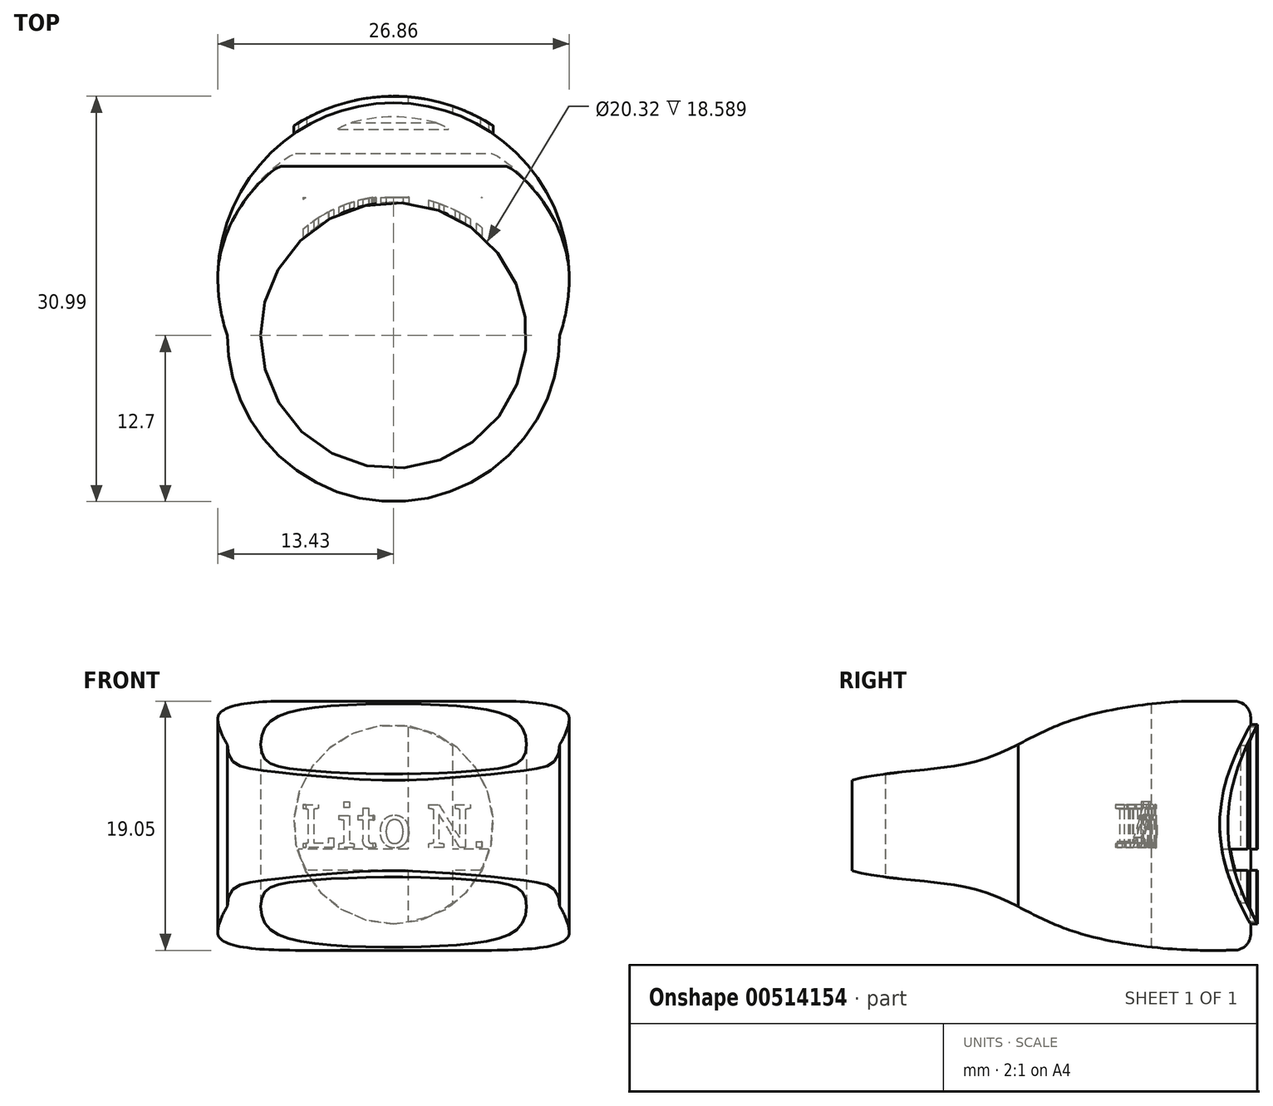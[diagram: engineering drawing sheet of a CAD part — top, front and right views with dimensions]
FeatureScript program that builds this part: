
annotation { "Feature Type Name" : "Feature", "Feature Type Description" : "" }
export const myFeature = defineFeature(function(context is Context, id is Id, definition is map)
    precondition{}
    {
        {
            var Q0;
            Q0=qCreatedBy(makeId("Top.planeOp"),FACE);
            var sketch = newSketch(context, id + "F0", { "sketchPlane" : qUnion([Q0])});
            skCircle(sketch, "E0", {"center": v(0, 0) * mm, "radius": 10.16 * mm});
            skArc(sketch, "E1", {"start": v(-12.7, 0) * mm, "mid": v(0, -12.7) * mm, "end": v(12.7, 0) * mm});
            skArc(sketch, "E2", {"start": v(12.7, 0) * mm, "mid": v(0, 17.78) * mm, "end": v(-12.7, 0) * mm});
            skSolve(sketch);
        }
        {
            var Q0;
            Q0=makeQuery(id+"F0.imprint","IMPRINT",FACE,{"disambiguationData":[TD([[makeQuery(id+"F0.imprint","IMPRINT",EDGE,{"derivedFrom":sQuery(id+"F0.wireOp",EDGE,"E0")}),-1.0]])]});
            extrude(context, id + "F1", {"entities" : qUnion([Q0]), "depth" : 19.05 * mm});
        }
        {
            var Q0;
            Q0=qCreatedBy(makeId("Front.planeOp"),FACE);
            var sketch = newSketch(context, id + "F2", { "sketchPlane" : qUnion([Q0])});
            skText(sketch, "E3", { "text": "Lito N.", "fontName": "RobotoSlab-Regular.ttf"});
            const initialGuessF2  = {"E3": [-0.00707, 0.00787, 1, 0, 0.0033]};
            skSetInitialGuess(sketch, initialGuessF2);
            skSolve(sketch);
        }
        {
            var Q0;
            Q0=qSketchRegion(id+"F2",true);
            var Q1;
            Q1=qConstructionFilter(qBodyType(qCreatedBy(id+"F2",EDGE),BodyType.WIRE),ConstructionObject.NO);
            extrude(context, id + "F3", {"entities" : qUnion([Q0]), "operationType" : NewBodyOperationType.REMOVE, "surfaceEntities" : qUnion([Q1]), "oppositeDirection" : true, "depth" : 11.23 * mm, "hasSecondDirection" : true, "secondDirectionOppositeDirection" : true, "secondDirectionDepth" : 7.24 * mm});
        }
        {
            var Q0;
            Q0=qCreatedBy(makeId("Top.planeOp"),FACE);
            var sketch = newSketch(context, id + "F4", { "sketchPlane" : qUnion([Q0])});
            skCircle(sketch, "E4", {"center": v(0, 0) * mm, "radius": 10.66 * mm});
            skCircle(sketch, "E5", {"center": v(0, 0) * mm, "radius": 12.5 * mm});
            skSolve(sketch);
        }
        {
            var Q0;
            Q0=makeQuery(id+"F4.imprint","IMPRINT",FACE,{"disambiguationData":[TD([[makeQuery(id+"F4.imprint","IMPRINT",EDGE,{"derivedFrom":sQuery(id+"F4.wireOp",EDGE,"E4")}),-1.0]])]});
            extrude(context, id + "F5", {"entities" : qUnion([Q0]), "operationType" : NewBodyOperationType.ADD, "depth" : 19.05 * mm});
        }
        {
            var Q0;
            Q0=makeQuery(id+"F1.opExtrude","CAP_EDGE",EDGE,{"disambiguationData":[OSD([sQuery(id+"F0.wireOp",EDGE,"E2")])],"isStart":false});
            var Q1;
            Q1=makeQuery(id+"F1.opExtrude","CAP_EDGE",EDGE,{"disambiguationData":[OSD([sQuery(id+"F0.wireOp",EDGE,"E2")])],"isStart":true});
            fillet(context, id + "F6", {"entities" : qUnion([Q0, Q1]), "radius" : 1.27 * mm, "tangentPropagation" : true, "allowEdgeOverflow" : false});
        }
        {
            var Q0;
            Q0=qCreatedBy(makeId("Right.planeOp"),FACE);
            var sketch = newSketch(context, id + "F7", { "sketchPlane" : qUnion([Q0])});
            skLineSegment(sketch, "E6", {"start": v(29.01, 9.54) * mm, "end": v(-18.1, 9.54) * mm});
            skFitSpline(sketch, "E7", {"points": [v(16.27, 19.07) * mm, v(3.6, 17.42) * mm, v(-3.17, 14.45) * mm, v(-12.74, 13) * mm], "startDerivative": vector(-34.03, 1.2) * mm, "endDerivative": vector(-25.58, -7.08) * mm});
            skLineSegment(sketch, "E8", {"start": v(16.27, 19.07) * mm, "end": v(19.29, 19.07) * mm});
            skLineSegment(sketch, "E9", {"start": v(19.29, 19.07) * mm, "end": v(19.29, 9.54) * mm});
            skLineSegment(sketch, "E10", {"start": v(-12.74, 13) * mm, "end": v(-12.8, 13) * mm});
            skLineSegment(sketch, "E11", {"start": v(-12.8, 13) * mm, "end": v(-12.8, 9.54) * mm});
            skLineSegment(sketch, "E12", {"start": v(21.42, 9.54) * mm, "end": v(21.42, 22.8) * mm});
            skLineSegment(sketch, "E13", {"start": v(21.42, 22.8) * mm, "end": v(-16.06, 22.8) * mm});
            skLineSegment(sketch, "E14", {"start": v(-16.06, 22.8) * mm, "end": v(-16.06, 9.54) * mm});
            skFitSpline(sketch, "E15.MirrorCS", {"points": [v(16.27, 0.01) * mm, v(3.6, 1.66) * mm, v(-3.17, 4.64) * mm, v(-12.74, 6.09) * mm], "startDerivative": vector(-34.03, -1.2) * mm, "endDerivative": vector(-25.58, 7.08) * mm});
            skLineSegment(sketch, "E16.MirrorCS", {"start": v(16.27, 0.01) * mm, "end": v(19.29, 0.01) * mm});
            skLineSegment(sketch, "E17.MirrorCS", {"start": v(19.29, 0.01) * mm, "end": v(19.29, 9.54) * mm});
            skLineSegment(sketch, "E18.MirrorCS", {"start": v(21.42, -3.71) * mm, "end": v(-16.06, -3.71) * mm});
            skLineSegment(sketch, "E19.MirrorCS", {"start": v(21.42, 9.54) * mm, "end": v(21.42, -3.71) * mm});
            skLineSegment(sketch, "E20.MirrorCS", {"start": v(-16.06, -3.71) * mm, "end": v(-16.06, 9.54) * mm});
            skLineSegment(sketch, "E21.MirrorCS", {"start": v(-12.8, 6.09) * mm, "end": v(-12.8, 9.54) * mm});
            skLineSegment(sketch, "E22.MirrorCS", {"start": v(-12.74, 6.09) * mm, "end": v(-12.8, 6.09) * mm});
            skSolve(sketch);
        }
        {
            var Q0;
            Q0=makeQuery(id+"F7.imprint","IMPRINT",FACE,{"disambiguationData":[TD([[makeQuery(id+"F7.imprint","IMPRINT",EDGE,{"derivedFrom":sQuery(id+"F7.wireOp",EDGE,"E7")}),-1.0]])]});
            var Q1;
            Q1=makeQuery(id+"F7.imprint","IMPRINT",FACE,{"disambiguationData":[TD([[makeQuery(id+"F7.imprint","IMPRINT",EDGE,{"derivedFrom":sQuery(id+"F7.wireOp",EDGE,"E15.MirrorCS")}),1.0]])]});
            extrude(context, id + "F8", {"entities" : qUnion([Q0, Q1]), "operationType" : NewBodyOperationType.REMOVE, "oppositeDirection" : true, "depth" : 25.4 * mm, "hasSecondDirection" : true, "secondDirectionOppositeDirection" : false, "secondDirectionDepth" : 25.4 * mm});
        }
        {
            var Q0;
            Q0=qCreatedBy(makeId("Front.planeOp"),FACE);
            var sketch = newSketch(context, id + "F9", { "sketchPlane" : qUnion([Q0])});
            skLineSegment(sketch, "E23", {"start": v(0, 15.75) * mm, "end": v(0, -9.15) * mm, "construction": true});
            skLineSegment(sketch, "E24", {"start": v(0, 9.63) * mm, "end": v(0, 1.35) * mm});
            skArc(sketch, "E25", {"start": v(1.1, 17.17) * mm, "mid": v(-5.67, 14.72) * mm, "end": v(-7.38, 7.74) * mm});
            skLineSegment(sketch, "E26", {"start": v(4.52, 15.64) * mm, "end": v(4.52, 7.74) * mm});
            skLineSegment(sketch, "E27", {"start": v(1.1, 2.2) * mm, "end": v(1.1, 6.1) * mm});
            skLineSegment(sketch, "E28", {"start": v(6.64, 6.1) * mm, "end": v(4.52, 6.1) * mm});
            skLineSegment(sketch, "E29", {"start": v(7.28, 7.74) * mm, "end": v(4.52, 7.74) * mm});
            skLineSegment(sketch, "E30.trimOffspring", {"start": v(1.1, 7.74) * mm, "end": v(-7.28, 7.74) * mm});
            skLineSegment(sketch, "E31.trimOffspring", {"start": v(1.1, 6.1) * mm, "end": v(-6.64, 6.1) * mm});
            skLineSegment(sketch, "E32.trimOffspring", {"start": v(4.52, 6.1) * mm, "end": v(4.52, 3.62) * mm});
            skArc(sketch, "E33.trimOffspring", {"start": v(7.38, 7.74) * mm, "mid": v(7.18, 12.19) * mm, "end": v(4.52, 15.76) * mm});
            skLineSegment(sketch, "E34.trimOffspring", {"start": v(1.1, 7.74) * mm, "end": v(1.1, 17.07) * mm});
            skArc(sketch, "E35.trimOffspring", {"start": v(-6.76, 6.1) * mm, "mid": v(-3.47, 2.85) * mm, "end": v(1.1, 2.09) * mm});
            skCircle(sketch, "E36", {"center": v(0, 9.63) * mm, "radius": 7.62 * mm});
            skCircle(sketch, "E37", {"center": v(0, 9.63) * mm, "radius": 7.52 * mm});
            skSolve(sketch);
        }
        {
            var Q0;
            {var subQ0=sQuery(id+"F9.wireOp",EDGE,"E26");Q0=makeQuery(id+"F9.imprint","IMPRINT",FACE,{"disambiguationData":[TD([[makeQuery(id+"F9.imprint","IMPRINT",EDGE,{"derivedFrom":subQ0}),1.0]])]});}
            var Q1;
            Q1=makeQuery(id+"F9.imprint","IMPRINT",FACE,{"disambiguationData":[TD([[makeQuery(id+"F9.imprint","IMPRINT",EDGE,{"derivedFrom":sQuery(id+"F9.wireOp",EDGE,"E36")}),1.0]])]});
            var Q2;
            {var subQ0=sQuery(id+"F9.wireOp",EDGE,"E34.trimOffspring");Q2=makeQuery(id+"F9.imprint","IMPRINT",FACE,{"disambiguationData":[TD([[makeQuery(id+"F9.imprint","IMPRINT",EDGE,{"derivedFrom":subQ0}),1.0]])]});}
            var Q3;
            {var subQ0=sQuery(id+"F9.wireOp",EDGE,"E28");Q3=makeQuery(id+"F9.imprint","IMPRINT",FACE,{"disambiguationData":[TD([[makeQuery(id+"F9.imprint","IMPRINT",EDGE,{"derivedFrom":subQ0}),1.0]])]});}
            var Q4;
            {var subQ5=sQuery(id+"F9.wireOp",EDGE,"E27");Q4=makeQuery(id+"F9.imprint","IMPRINT",FACE,{"disambiguationData":[TD([[makeQuery(id+"F9.imprint","IMPRINT",EDGE,{"derivedFrom":subQ5}),1.0]])]});}
            var Q5;
            {var subQ0=sQuery(id+"F9.wireOp",EDGE,"E37");var subQ1=sQuery(id+"F9.wireOp",EDGE,"E24");var subQ2=makeQuery(id+"F9.imprint","INTERSECT",VERTEX,{"derivedFrom":[subQ1,subQ0]});Q5=makeQuery(id+"F9.imprint","IMPRINT",FACE,{"disambiguationData":[TD([[makeQuery(id+"F9.imprint","IMPRINT",EDGE,{"disambiguationData":[TD([[subQ2,1.0]])],"derivedFrom":subQ1}),-1.0]])]});}
            extrude(context, id + "F10", {"entities" : qUnion([Q0, Q1, Q2, Q3, Q4, Q5]), "operationType" : NewBodyOperationType.ADD, "oppositeDirection" : true, "depth" : 20.32 * mm, "hasSecondDirection" : true, "secondDirectionOppositeDirection" : true, "secondDirectionDepth" : 10.54 * mm});
        }
        {
            var Q0;
            Q0=qCreatedBy(makeId("Top.planeOp"),FACE);
            var sketch = newSketch(context, id + "F11", { "sketchPlane" : qUnion([Q0])});
            skArc(sketch, "E38", {"start": v(13.2, 0) * mm, "mid": v(0, 18.29) * mm, "end": v(-13.2, 0) * mm});
            skLineSegment(sketch, "E39", {"start": v(13.2, 0) * mm, "end": v(15.4, 0) * mm});
            skLineSegment(sketch, "E40", {"start": v(15.4, 0) * mm, "end": v(15.4, 21.9) * mm});
            skLineSegment(sketch, "E41", {"start": v(15.4, 21.9) * mm, "end": v(-16.46, 21.9) * mm});
            skLineSegment(sketch, "E42", {"start": v(-16.46, 21.9) * mm, "end": v(-16.46, 0) * mm});
            skLineSegment(sketch, "E43", {"start": v(-16.46, 0) * mm, "end": v(-13.2, 0) * mm});
            skSolve(sketch);
        }
        {
            var Q0;
            Q0=makeQuery(id+"F11.imprint","IMPRINT",FACE,{"disambiguationData":[TD([[makeQuery(id+"F11.imprint","IMPRINT",EDGE,{"derivedFrom":sQuery(id+"F11.wireOp",EDGE,"E38")}),-1.0]])]});
            extrude(context, id + "F12", {"entities" : qUnion([Q0]), "operationType" : NewBodyOperationType.REMOVE, "depth" : 25.4 * mm});
        }
    });
